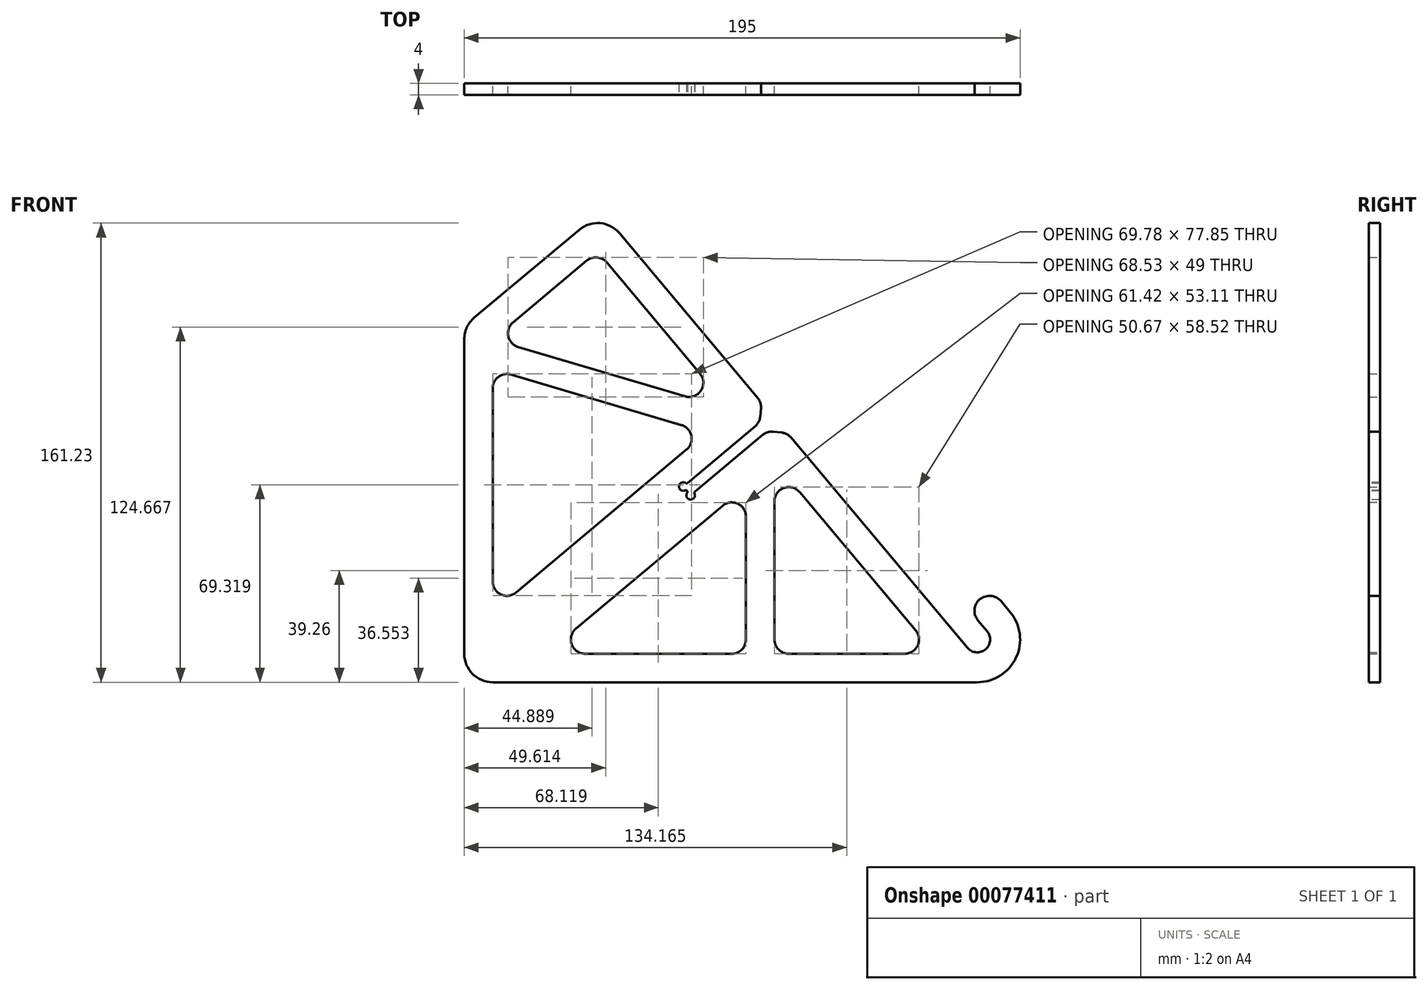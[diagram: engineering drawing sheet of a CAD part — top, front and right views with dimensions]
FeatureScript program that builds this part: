
annotation { "Feature Type Name" : "Feature", "Feature Type Description" : "" }
export const myFeature = defineFeature(function(context is Context, id is Id, definition is map)
    precondition{}
    {
        {
            var Q0;
            Q0=qCreatedBy(makeId("Front.planeOp"),FACE);
            var sketch = newSketch(context, id + "F0", { "sketchPlane" : qUnion([Q0])});
            skArc(sketch, "E0", {"start": v(-3.45, -2.9) * mm, "mid": v(2.9, -3.45) * mm, "end": v(3.45, 2.9) * mm});
            skLineSegment(sketch, "E1", {"start": v(3.45, 2.9) * mm, "end": v(0.23, 6.72) * mm});
            skArc(sketch, "E2", {"start": v(8.28, 13.47) * mm, "mid": v(0.88, 14.12) * mm, "end": v(0.23, 6.72) * mm});
            skLineSegment(sketch, "E3", {"start": v(8.28, 13.47) * mm, "end": v(11.5, 9.64) * mm});
            skArc(sketch, "E4", {"start": v(0, -15) * mm, "mid": v(13.6, -6.34) * mm, "end": v(11.5, 9.64) * mm});
            skLineSegment(sketch, "E5", {"start": v(0, -15) * mm, "end": v(-170, -15) * mm});
            skLineSegment(sketch, "E6", {"start": v(-3.45, -2.9) * mm, "end": v(-69.94, 76.35) * mm});
            skLineSegment(sketch, "E7", {"start": v(-180, -5) * mm, "end": v(-180, 105.38) * mm});
            skLineSegment(sketch, "E8", {"start": v(-176.43, 113.04) * mm, "end": v(-139.67, 143.89) * mm});
            skPoint(sketch, "E9.visualSharp", {"position": v(-132, 150.32) * mm});
            skArc(sketch, "E9.filletArc", {"start": v(-125.58, 142.66) * mm, "mid": v(-132.37, 146.19) * mm, "end": v(-139.67, 143.89) * mm});
            skPoint(sketch, "E10.visualSharp", {"position": v(-180, 110.04) * mm});
            skArc(sketch, "E10.filletArc", {"start": v(-176.43, 113.04) * mm, "mid": v(-179.06, 109.6) * mm, "end": v(-180, 105.38) * mm});
            skPoint(sketch, "E11.visualSharp", {"position": v(-180, -15) * mm});
            skArc(sketch, "E11.filletArc", {"start": v(-180, -5) * mm, "mid": v(-177.07, -12.07) * mm, "end": v(-170, -15) * mm});
            skLineSegment(sketch, "E12", {"start": v(-72.51, 79.41) * mm, "end": v(-103.15, 53.7) * mm});
            skLineSegment(sketch, "E13", {"start": v(-103.15, 53.7) * mm, "end": v(-100.58, 50.64) * mm});
            skLineSegment(sketch, "E14", {"start": v(-100.58, 50.64) * mm, "end": v(-69.94, 76.35) * mm});
            skLineSegment(sketch, "E15.trimOffspring", {"start": v(-72.51, 79.41) * mm, "end": v(-125.58, 142.66) * mm});
            skLineSegment(sketch, "E16", {"start": v(-101.87, 52.17) * mm, "end": v(-170, -5) * mm, "construction": true});
            skSolve(sketch);
        }
        {
            var Q0;
            Q0=makeQuery(id+"F0.imprint","IMPRINT",FACE,{"disambiguationData":[TD([[makeQuery(id+"F0.imprint","IMPRINT",EDGE,{"derivedFrom":sQuery(id+"F0.wireOp",EDGE,"E0")}),-1.0]])]});
            extrude(context, id + "F1", {"entities" : qUnion([Q0]), "endBound" : BoundingType.SYMMETRIC, "depth" : 4 * mm});
        }
        {
            var Q0;
            Q0=makeQuery(id+"F1.opExtrude","SWEPT_EDGE",EDGE,{"disambiguationData":[OSD([sQuery(id+"F0.wireOp",EDGE,"E12"),sQuery(id+"F0.wireOp",EDGE,"E15.trimOffspring")])]});
            var Q1;
            Q1=makeQuery(id+"F1.opExtrude","SWEPT_EDGE",EDGE,{"disambiguationData":[OSD([sQuery(id+"F0.wireOp",EDGE,"E6"),sQuery(id+"F0.wireOp",EDGE,"E14")])]});
            chamfer(context, id + "F2", {"entities" : qUnion([Q0, Q1]), "width" : 5 * mm, "tangentPropagation" : true});
        }
        {
            var Q0;
            {var subQ0=sQuery(id+"F0.wireOp",EDGE,"E15.trimOffspring");Q0=makeQuery(id+"F2.opChamfer","BLEND_EDGE",EDGE,{"blendedFrom":[makeQuery(id+"F1.opExtrude","SWEPT_EDGE",EDGE,{"disambiguationData":[OSD([sQuery(id+"F0.wireOp",EDGE,"E12"),subQ0])]}),makeQuery(id+"F1.opExtrude","SWEPT_FACE",FACE,{"disambiguationData":[OSD([subQ0])]})],"blendedInto":[makeQuery(id+"F1.opExtrude","SWEPT_FACE",FACE,{"disambiguationData":[OSD([subQ0])]})]});}
            var Q1;
            {var subQ0=sQuery(id+"F0.wireOp",EDGE,"E12");Q1=makeQuery(id+"F2.opChamfer","BLEND_EDGE",EDGE,{"blendedFrom":[makeQuery(id+"F1.opExtrude","SWEPT_EDGE",EDGE,{"disambiguationData":[OSD([subQ0,sQuery(id+"F0.wireOp",EDGE,"E15.trimOffspring")])]}),makeQuery(id+"F1.opExtrude","SWEPT_FACE",FACE,{"disambiguationData":[OSD([subQ0])]})],"blendedInto":[makeQuery(id+"F1.opExtrude","SWEPT_FACE",FACE,{"disambiguationData":[OSD([subQ0])]})]});}
            var Q2;
            {var subQ0=sQuery(id+"F0.wireOp",EDGE,"E14");Q2=makeQuery(id+"F2.opChamfer","BLEND_EDGE",EDGE,{"blendedFrom":[makeQuery(id+"F1.opExtrude","SWEPT_EDGE",EDGE,{"disambiguationData":[OSD([sQuery(id+"F0.wireOp",EDGE,"E6"),subQ0])]}),makeQuery(id+"F1.opExtrude","SWEPT_FACE",FACE,{"disambiguationData":[OSD([subQ0])]})],"blendedInto":[makeQuery(id+"F1.opExtrude","SWEPT_FACE",FACE,{"disambiguationData":[OSD([subQ0])]})]});}
            var Q3;
            {var subQ0=sQuery(id+"F0.wireOp",EDGE,"E6");Q3=makeQuery(id+"F2.opChamfer","BLEND_EDGE",EDGE,{"blendedFrom":[makeQuery(id+"F1.opExtrude","SWEPT_EDGE",EDGE,{"disambiguationData":[OSD([subQ0,sQuery(id+"F0.wireOp",EDGE,"E14")])]}),makeQuery(id+"F1.opExtrude","SWEPT_FACE",FACE,{"disambiguationData":[OSD([subQ0])]})],"blendedInto":[makeQuery(id+"F1.opExtrude","SWEPT_FACE",FACE,{"disambiguationData":[OSD([subQ0])]})]});}
            fillet(context, id + "F3", {"entities" : qUnion([Q0, Q1, Q2, Q3]), "radius" : 5 * mm, "tangentPropagation" : true, "allowEdgeOverflow" : false});
        }
        {
            var Q0;
            Q0=makeQuery(id+"F1.opExtrude","CAP_FACE",FACE,{"disambiguationData":[OSD([sQuery(id+"F0.wireOp",EDGE,"E0"),sQuery(id+"F0.wireOp",EDGE,"E1"),sQuery(id+"F0.wireOp",EDGE,"E2"),sQuery(id+"F0.wireOp",EDGE,"E3"),sQuery(id+"F0.wireOp",EDGE,"E4"),sQuery(id+"F0.wireOp",EDGE,"E5"),sQuery(id+"F0.wireOp",EDGE,"E6"),sQuery(id+"F0.wireOp",EDGE,"E7"),sQuery(id+"F0.wireOp",EDGE,"E8"),sQuery(id+"F0.wireOp",EDGE,"E9.filletArc"),sQuery(id+"F0.wireOp",EDGE,"E10.filletArc"),sQuery(id+"F0.wireOp",EDGE,"E11.filletArc"),sQuery(id+"F0.wireOp",EDGE,"E12"),sQuery(id+"F0.wireOp",EDGE,"E13"),sQuery(id+"F0.wireOp",EDGE,"E14"),sQuery(id+"F0.wireOp",EDGE,"E15.trimOffspring")])],"isStart":false});
            var sketch = newSketch(context, id + "F4", { "sketchPlane" : qUnion([Q0])});
            skCircle(sketch, "E17", {"center": v(-103.15, 53.7) * mm, "radius": 1.5 * mm});
            skCircle(sketch, "E18", {"center": v(-100.58, 50.64) * mm, "radius": 1.5 * mm});
            skSolve(sketch);
        }
        {
            var Q0;
            Q0 = qSketchRegion(id + "F4", true);
            extrude(context, id + "F5", {"entities" : qUnion([Q0]), "operationType" : NewBodyOperationType.REMOVE, "endBound" : BoundingType.THROUGH_ALL, "oppositeDirection" : true, "depth" : 25 * mm});
        }
        {
            var Q0;
            Q0=makeQuery(id+"F5.boolean.opBoolean","INTERSECT",EDGE,{"derivedFrom":[makeQuery(id+"F1.opExtrude","SWEPT_FACE",FACE,{"disambiguationData":[OSD([sQuery(id+"F0.wireOp",EDGE,"E12")])]}),makeQuery(id+"F5.opExtrude","SWEPT_FACE",FACE,{"disambiguationData":[OSD([sQuery(id+"F4.wireOp",EDGE,"E17")])]})]});
            var Q1;
            Q1=makeQuery(id+"F5.boolean.opBoolean","INTERSECT",EDGE,{"derivedFrom":[makeQuery(id+"F1.opExtrude","SWEPT_FACE",FACE,{"disambiguationData":[OSD([sQuery(id+"F0.wireOp",EDGE,"E14")])]}),makeQuery(id+"F5.opExtrude","SWEPT_FACE",FACE,{"disambiguationData":[OSD([sQuery(id+"F4.wireOp",EDGE,"E18")])]})]});
            fillet(context, id + "F6", {"entities" : qUnion([Q0, Q1]), "radius" : 0.5 * mm, "tangentPropagation" : true, "allowEdgeOverflow" : false});
        }
        {
            var Q0;
            Q0=makeQuery(id+"F5.boolean.opBoolean","INTERSECT",EDGE,{"derivedFrom":[makeQuery(id+"F1.opExtrude","SWEPT_FACE",FACE,{"disambiguationData":[OSD([sQuery(id+"F0.wireOp",EDGE,"E13")])]}),makeQuery(id+"F5.opExtrude","SWEPT_FACE",FACE,{"disambiguationData":[OSD([sQuery(id+"F4.wireOp",EDGE,"E17")])]})]});
            var Q1;
            Q1=makeQuery(id+"F5.boolean.opBoolean","INTERSECT",EDGE,{"derivedFrom":[makeQuery(id+"F1.opExtrude","SWEPT_FACE",FACE,{"disambiguationData":[OSD([sQuery(id+"F0.wireOp",EDGE,"E13")])]}),makeQuery(id+"F5.opExtrude","SWEPT_FACE",FACE,{"disambiguationData":[OSD([sQuery(id+"F4.wireOp",EDGE,"E18")])]})]});
            fillet(context, id + "F7", {"entities" : qUnion([Q0, Q1]), "radius" : 0.5 * mm, "tangentPropagation" : true, "allowEdgeOverflow" : false});
        }
        {
            var Q0;
            Q0=makeQuery(id+"F1.opExtrude","CAP_FACE",FACE,{"disambiguationData":[OSD([sQuery(id+"F0.wireOp",EDGE,"E0"),sQuery(id+"F0.wireOp",EDGE,"E1"),sQuery(id+"F0.wireOp",EDGE,"E2"),sQuery(id+"F0.wireOp",EDGE,"E3"),sQuery(id+"F0.wireOp",EDGE,"E4"),sQuery(id+"F0.wireOp",EDGE,"E5"),sQuery(id+"F0.wireOp",EDGE,"E6"),sQuery(id+"F0.wireOp",EDGE,"E7"),sQuery(id+"F0.wireOp",EDGE,"E8"),sQuery(id+"F0.wireOp",EDGE,"E9.filletArc"),sQuery(id+"F0.wireOp",EDGE,"E10.filletArc"),sQuery(id+"F0.wireOp",EDGE,"E11.filletArc"),sQuery(id+"F0.wireOp",EDGE,"E12"),sQuery(id+"F0.wireOp",EDGE,"E13"),sQuery(id+"F0.wireOp",EDGE,"E14"),sQuery(id+"F0.wireOp",EDGE,"E15.trimOffspring")])],"isStart":true});
            var sketch = newSketch(context, id + "F8", { "sketchPlane" : qUnion([Q0])});
            skLineSegment(sketch, "E19", {"start": v(21.63, 3.21) * mm, "end": v(62.34, 51.74) * mm});
            skLineSegment(sketch, "E20", {"start": v(71.17, 48.52) * mm, "end": v(71.17, 0) * mm});
            skLineSegment(sketch, "E21", {"start": v(66.17, -5) * mm, "end": v(25.46, -5) * mm});
            skLineSegment(sketch, "E22", {"start": v(81.17, 0) * mm, "end": v(81.17, 43.15) * mm});
            skLineSegment(sketch, "E23", {"start": v(89.39, 46.98) * mm, "end": v(140.8, 3.83) * mm});
            skLineSegment(sketch, "E24", {"start": v(137.6, -5) * mm, "end": v(86.17, -5) * mm});
            skLineSegment(sketch, "E25", {"start": v(97.28, 93.38) * mm, "end": v(130.02, 132.4) * mm});
            skLineSegment(sketch, "E26", {"start": v(137.07, 133.01) * mm, "end": v(162.87, 111.36) * mm});
            skLineSegment(sketch, "E27", {"start": v(161.08, 102.74) * mm, "end": v(102.54, 85.37) * mm});
            skLineSegment(sketch, "E28", {"start": v(102, 66.7) * mm, "end": v(161.79, 16.52) * mm});
            skLineSegment(sketch, "E29", {"start": v(170, 20.35) * mm, "end": v(170, 88.25) * mm});
            skLineSegment(sketch, "E30", {"start": v(163.58, 93.05) * mm, "end": v(103.79, 75.31) * mm});
            skPoint(sketch, "E31.visualSharp", {"position": v(133.24, 136.23) * mm});
            skArc(sketch, "E31.filletArc", {"start": v(137.07, 133.01) * mm, "mid": v(133.42, 134.16) * mm, "end": v(130.02, 132.4) * mm});
            skPoint(sketch, "E32.visualSharp", {"position": v(170, 105.38) * mm});
            skArc(sketch, "E32.filletArc", {"start": v(161.08, 102.74) * mm, "mid": v(164.56, 106.51) * mm, "end": v(162.87, 111.36) * mm});
            skPoint(sketch, "E33.visualSharp", {"position": v(170, 94.95) * mm});
            skArc(sketch, "E33.filletArc", {"start": v(170, 88.25) * mm, "mid": v(168, 92.26) * mm, "end": v(163.58, 93.05) * mm});
            skPoint(sketch, "E34.visualSharp", {"position": v(170, 9.63) * mm});
            skArc(sketch, "E34.filletArc", {"start": v(161.79, 16.52) * mm, "mid": v(167.11, 15.82) * mm, "end": v(170, 20.35) * mm});
            skPoint(sketch, "E35.visualSharp", {"position": v(94.87, 72.67) * mm});
            skArc(sketch, "E35.filletArc", {"start": v(103.79, 75.31) * mm, "mid": v(100.32, 71.54) * mm, "end": v(102, 66.7) * mm});
            skPoint(sketch, "E36.visualSharp", {"position": v(86.6, 80.65) * mm});
            skArc(sketch, "E36.filletArc", {"start": v(97.28, 93.38) * mm, "mid": v(96.93, 87.42) * mm, "end": v(102.54, 85.37) * mm});
            skPoint(sketch, "E37.visualSharp", {"position": v(151.33, -5) * mm});
            skArc(sketch, "E37.filletArc", {"start": v(137.6, -5) * mm, "mid": v(142.3, -1.71) * mm, "end": v(140.8, 3.83) * mm});
            skPoint(sketch, "E38.visualSharp", {"position": v(81.17, 53.87) * mm});
            skArc(sketch, "E38.filletArc", {"start": v(89.39, 46.98) * mm, "mid": v(84.06, 47.68) * mm, "end": v(81.17, 43.15) * mm});
            skPoint(sketch, "E39.visualSharp", {"position": v(81.17, -5) * mm});
            skArc(sketch, "E39.filletArc", {"start": v(81.17, 0) * mm, "mid": v(82.64, -3.54) * mm, "end": v(86.17, -5) * mm});
            skPoint(sketch, "E40.visualSharp", {"position": v(71.17, 62.26) * mm});
            skArc(sketch, "E40.filletArc", {"start": v(71.17, 48.52) * mm, "mid": v(67.88, 53.22) * mm, "end": v(62.34, 51.74) * mm});
            skPoint(sketch, "E41.visualSharp", {"position": v(14.73, -5) * mm});
            skArc(sketch, "E41.filletArc", {"start": v(21.63, 3.21) * mm, "mid": v(20.92, -2.11) * mm, "end": v(25.46, -5) * mm});
            skPoint(sketch, "E42.visualSharp", {"position": v(71.17, -5) * mm});
            skArc(sketch, "E42.filletArc", {"start": v(66.17, -5) * mm, "mid": v(69.7, -3.54) * mm, "end": v(71.17, 0) * mm});
            skSolve(sketch);
        }
        {
            var Q0;
            Q0=makeQuery(id+"F8.imprint","IMPRINT",FACE,{"disambiguationData":[TD([[makeQuery(id+"F8.imprint","IMPRINT",EDGE,{"derivedFrom":sQuery(id+"F8.wireOp",EDGE,"E25")}),-1.0]])]});
            var Q1;
            Q1=makeQuery(id+"F8.imprint","IMPRINT",FACE,{"disambiguationData":[TD([[makeQuery(id+"F8.imprint","IMPRINT",EDGE,{"derivedFrom":sQuery(id+"F8.wireOp",EDGE,"E28")}),1.0]])]});
            var Q2;
            Q2=makeQuery(id+"F8.imprint","IMPRINT",FACE,{"disambiguationData":[TD([[makeQuery(id+"F8.imprint","IMPRINT",EDGE,{"derivedFrom":sQuery(id+"F8.wireOp",EDGE,"E22")}),-1.0]])]});
            var Q3;
            Q3=makeQuery(id+"F8.imprint","IMPRINT",FACE,{"disambiguationData":[TD([[makeQuery(id+"F8.imprint","IMPRINT",EDGE,{"derivedFrom":sQuery(id+"F8.wireOp",EDGE,"E19")}),-1.0]])]});
            extrude(context, id + "F9", {"entities" : qUnion([Q0, Q1, Q2, Q3]), "operationType" : NewBodyOperationType.REMOVE, "endBound" : BoundingType.THROUGH_ALL, "oppositeDirection" : true, "depth" : 25 * mm});
        }
    });
